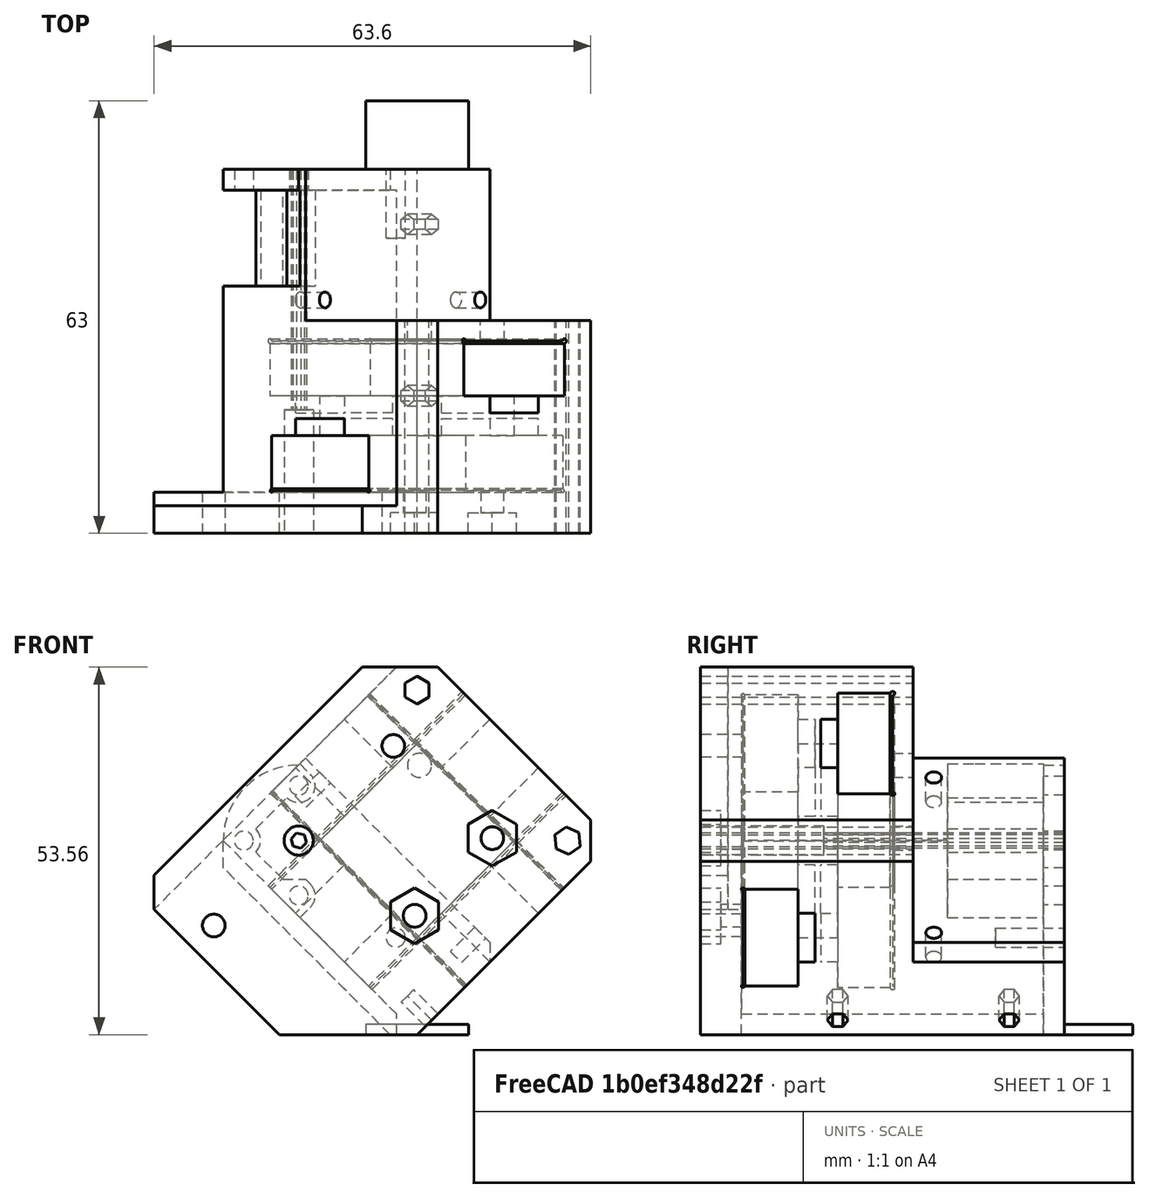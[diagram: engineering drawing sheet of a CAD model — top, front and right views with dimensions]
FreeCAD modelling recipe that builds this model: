
FCSTD DOCUMENT  (FreeCAD 0.19R)
Label: middle
License: All rights reserved
LicenseURL: http://en.wikipedia.org/wiki/All_rights_reserved
objects: Sketcher::SketchObject×25, PartDesign::Pocket×18, PartDesign::Pad×5, PartDesign::Body×1, Mesh::Feature×1
note: 72 computed .brp shape members not serialized (recipe doc carries the construction recipe); baked Part::Feature solids carry a one-line shape summary decoded from their .brp

FEATURE [Sketcher::SketchObject] Sketch  label="Body001"
  FullyConstrained = true
  MapMode = 5
  Support = -> [XY_Plane]
  sketch-geometry (11):
    g0: LineSegment StartX=20 StartY=15.7574 StartZ=0 EndX=20 EndY=-15.7574 EndZ=0
    g1: LineSegment StartX=15.7574 StartY=-20 StartZ=0 EndX=-20 EndY=-20 EndZ=0
    g2: LineSegment StartX=-20 StartY=-15.7574 StartZ=0 EndX=-20 EndY=19.9515 EndZ=0
    g3: Circle CenterX=-12.1976 CenterY=12.1976 CenterZ=0 NormalX=0 NormalY=0 NormalZ=1 AngleXU=0 Radius=2.1
    g4: LineSegment StartX=-12.1976 StartY=12.1976 StartZ=0 EndX=0 EndY=0 EndZ=0
    g5: ArcOfCircle CenterX=-12.1976 CenterY=12.1976 CenterZ=0 NormalX=0 NormalY=0 NormalZ=1 AngleXU=0 Radius=11 StartAngle=0.788519 EndAngle=2.35931
    g6: LineSegment StartX=-4.44373 StartY=20 StartZ=0 EndX=15.7574 EndY=20 EndZ=0
    g7: LineSegment StartX=15.7574 StartY=-20 StartZ=0 EndX=20 EndY=-15.7574 EndZ=0
    g8: LineSegment StartX=-20 StartY=-15.7574 StartZ=0 EndX=-22.1213 EndY=-17.8787 EndZ=0
    g9: LineSegment StartX=-22.1213 StartY=-17.8787 StartZ=0 EndX=-20 EndY=-20 EndZ=0
    g10: LineSegment StartX=15.7574 StartY=20 StartZ=0 EndX=20 EndY=15.7574 EndZ=0
  constraints (32):
    c: Horizontal(g1)
    c: Vertical(g0)
    c: Vertical(g2)
    c: Distance(g-1,g3) = 17.25
    c: Coincident(g4,g3)
    c: Coincident(g4,g-1)
    c: Angle(g4) = -0.785398
    c: Diameter(g3) = 4.2
    c: Coincident(g5,g3)
    c: Diameter(g5) = 22
    c: DistanceX(g1) = -20
    c: Coincident(g6,g5)
    c: Horizontal(g6)
    c: Coincident(g5,g2)
    c: Coincident(g7,g1)
    c: Coincident(g7,g0)
    c: Angle(g7) = 0.785398
    c: Distance(g7) = 6
    c: DistanceY(g1) = -20
    c: Coincident(g2,g8)
    c: Coincident(g8,g9)
    c: Coincident(g9,g1)
    c: Angle(g9) = -0.785398
    c: Angle(g8) = -2.35619
    c: Distance(g9) = 3
    c: DistanceX(g2) = -20
    c: Coincident(g10,g6)
    c: Coincident(g10,g0)
    c: Distance(g10) = 6
    c: Angle(g10) = -0.785398
    c: DistanceX(g0) = 20
    c: DistanceY(g6) = 20
FEATURE [PartDesign::Pad] Pad
  Direction = (1,1,1)
  Length = 53
  Length2 = 10
  Profile = -> Sketch
  Reversed = true
  Type = 0
FEATURE [Sketcher::SketchObject] Sketch001  label="RailHole"
  FullyConstrained = true
  MapMode = 5
  Placement = pos=(20,0,0) rot=(0.57735,0.57735,0.57735;2.0944rad)
  Support = -> [Pad]
  sketch-geometry (10):
    g0: LineSegment StartX=-10.35 StartY=-27.65 StartZ=0 EndX=-10.35 EndY=-20 EndZ=0
    g1: LineSegment StartX=5 StartY=-17.5 StartZ=0 EndX=-5 EndY=-17.5 EndZ=0
    g2: LineSegment StartX=10 StartY=-28 StartZ=0 EndX=-10 EndY=-28 EndZ=0
    g3: LineSegment StartX=5 StartY=-17.5 StartZ=0 EndX=5 EndY=-20 EndZ=0
    g4: LineSegment StartX=-5 StartY=-20 StartZ=0 EndX=-5 EndY=-17.5 EndZ=0
    g5: LineSegment StartX=-10.35 StartY=-20 StartZ=0 EndX=-5 EndY=-20 EndZ=0
    g6: LineSegment StartX=5 StartY=-20 StartZ=0 EndX=10.3495 EndY=-20 EndZ=0
    g7: LineSegment StartX=10.3495 StartY=-27.65 StartZ=0 EndX=10.3495 EndY=-20 EndZ=0
    g8: ArcOfCircle CenterX=-10.35 CenterY=-28 CenterZ=0 NormalX=0 NormalY=0 NormalZ=1 AngleXU=0 Radius=0.35 StartAngle=1.5708 EndAngle=6.28319
    g9: ArcOfCircle CenterX=10.35 CenterY=-28 CenterZ=0 NormalX=0 NormalY=0 NormalZ=1 AngleXU=0 Radius=0.35 StartAngle=3.14159 EndAngle=7.85541
  constraints (29):
    c: Vertical(g0)
    c: Symmetric(g1,g1,g-2)
    c: Distance(g1) = 10
    c: Coincident(g1,g3)
    c: Vertical(g3)
    c: Coincident(g4,g1)
    c: Symmetric(g3,g4,g-2)
    c: Distance(g3) = 2.5
    c: Distance(g2) = 20
    c: Coincident(g5,g4)
    c: Horizontal(g5)
    c: Coincident(g3,g6)
    c: Horizontal(g6)
    c: Vertical(g7)
    c: Coincident(g0,g5)
    c: Coincident(g7,g6)
    c: Coincident(g0,g8)
    c: Coincident(g8,g2)
    c: Diameter(g8) = 0.7
    c: DistanceX(g0,g8) = 0
    c: DistanceY(g2,g8) = 0
    c: Coincident(g9,g2)
    c: Coincident(g9,g7)
    c: Diameter(g9) = 0.7
    c: DistanceY(g2,g9) = 0
    c: DistanceX(g7,g9) = 0.0005
    c: Symmetric(g9,g8,g-2)
    c: Distance(g9,g6) = 8
    c: DistanceY(g8) = -28
FEATURE [PartDesign::Pocket] Pocket
  BaseFeature = -> Pad
  Length = 5
  Length2 = 100
  Profile = -> Sketch001
  Type = 1
FEATURE [Sketcher::SketchObject] Sketch008  label="ExtruderHole"
  FullyConstrained = false
  MapMode = 5
  Placement = pos=(0,0,4) rot=(0,0,1;0rad)
  sketch-geometry (2):
    g0: LineSegment StartX=0 StartY=0 StartZ=0 EndX=-54.6242 EndY=54.6242 EndZ=0
    g1: Circle CenterX=-12.1976 CenterY=12.1976 CenterZ=0 NormalX=0 NormalY=0 NormalZ=1 AngleXU=0 Radius=0.75
  constraints (5):
    c: Coincident(g0,g-1)
    c: Angle(g0) = 2.35619
    c: PointOnObject(g1,g0)
    c: Distance(g-1,g1) = 17.25
    c: Diameter(g1) = 1.5
FEATURE [Sketcher::SketchObject] Sketch009  label="reference"
  FullyConstrained = false
  MapMode = 5
  Placement = pos=(0,0,-25) rot=(1,0,0;3.14159rad)
  sketch-geometry (2):
    g0: Circle CenterX=-12.0208 CenterY=-12.0208 CenterZ=0 NormalX=0 NormalY=0 NormalZ=1 AngleXU=0 Radius=10
    g1: LineSegment StartX=0 StartY=0 StartZ=0 EndX=-27.7674 EndY=-27.7674 EndZ=0
  constraints (5):
    c: Diameter(g0) = 20
    c: Coincident(g1,g-1)
    c: Angle(g1) = -2.35619
    c: PointOnObject(g0,g1)
    c: Distance(g0,g1) = 17
FEATURE [Sketcher::SketchObject] Sketch010  label="reference2"
  FullyConstrained = false
  MapMode = 5
  Placement = pos=(0,0,-37) rot=(1,0,0;3.14159rad)
  sketch-geometry (2):
    g0: Circle CenterX=-12.1976 CenterY=-12.1976 CenterZ=0 NormalX=0 NormalY=0 NormalZ=1 AngleXU=0 Radius=8
    g1: LineSegment StartX=0 StartY=0 StartZ=0 EndX=-38.1566 EndY=-38.1566 EndZ=0
  constraints (5):
    c: Diameter(g0) = 16
    c: Coincident(g1,g-1)
    c: Angle(g1) = -2.35619
    c: Distance(g0,g1) = 17.25
    c: PointOnObject(g0,g1)
FEATURE [Sketcher::SketchObject] Sketch021  label="InternalTri"
  FullyConstrained = true
  MapMode = 5
  Placement = pos=(0,-3e-15,-12) rot=(0,0,1;0rad)
  sketch-geometry (4):
    g0: LineSegment StartX=-10 StartY=10 StartZ=0 EndX=10 EndY=10 EndZ=0
    g1: LineSegment StartX=10 StartY=10 StartZ=0 EndX=10 EndY=-10 EndZ=0
    g2: LineSegment StartX=10 StartY=-10 StartZ=0 EndX=-10 EndY=-10 EndZ=0
    g3: LineSegment StartX=-10 StartY=-10 StartZ=0 EndX=-10 EndY=10 EndZ=0
  constraints (11):
    c: Coincident(g0,g1)
    c: Coincident(g1,g2)
    c: Coincident(g2,g3)
    c: Coincident(g3,g0)
    c: Horizontal(g0)
    c: Horizontal(g2)
    c: Vertical(g1)
    c: Vertical(g3)
    c: Symmetric(g1,g0,g-1)
    c: Equal(g1,g0)
    c: Distance(g1) = 20
FEATURE [PartDesign::Pocket] Pocket002
  BaseFeature = -> Pocket
  Length = 10
  Length2 = 2
  Profile = -> Sketch021
  Type = 4
FEATURE [Sketcher::SketchObject] Sketch019  label="RailHole2"
  FullyConstrained = true
  MapMode = 5
  Placement = pos=(0,-20,0) rot=(1,0,0;1.5708rad)
  Support = -> [Pocket002]
  sketch-geometry (10):
    g0: LineSegment StartX=-9.75 StartY=-6.2 StartZ=0 EndX=9.75 EndY=-6.2 EndZ=0
    g1: LineSegment StartX=10 StartY=-14.2 StartZ=0 EndX=5 EndY=-14.2 EndZ=0
    g2: LineSegment StartX=5 StartY=-14.2 StartZ=0 EndX=5 EndY=-16.7 EndZ=0
    g3: LineSegment StartX=5 StartY=-16.7 StartZ=0 EndX=-5 EndY=-16.7 EndZ=0
    g4: LineSegment StartX=-5 StartY=-16.7 StartZ=0 EndX=-5 EndY=-14.2 EndZ=0
    g5: LineSegment StartX=-5 StartY=-14.2 StartZ=0 EndX=-10 EndY=-14.2 EndZ=0
    g6: ArcOfCircle CenterX=10 CenterY=-6.2 CenterZ=0 NormalX=0 NormalY=0 NormalZ=1 AngleXU=0 Radius=0.25 StartAngle=4.71239 EndAngle=9.42478
    g7: ArcOfCircle CenterX=-10 CenterY=-6.2 CenterZ=0 NormalX=0 NormalY=0 NormalZ=1 AngleXU=0 Radius=0.25 StartAngle=-9e-16 EndAngle=4.71239
    g8: LineSegment StartX=-10 StartY=-14.2 StartZ=0 EndX=-10 EndY=-6.45 EndZ=0
    g9: LineSegment StartX=10 StartY=-14.2 StartZ=0 EndX=10 EndY=-6.45 EndZ=0
  constraints (29):
    c: Horizontal(g0)
    c: Horizontal(g1)
    c: Coincident(g1,g2)
    c: Vertical(g2)
    c: Coincident(g2,g3)
    c: Horizontal(g3)
    c: Coincident(g3,g4)
    c: Vertical(g4)
    c: Coincident(g4,g5)
    c: Symmetric(g1,g5,g-2)
    c: Distance(g3) = 10
    c: Symmetric(g4,g1,g-2)
    c: DistanceY(g0) = -6.2
    c: Distance(g2) = 2.5
    c: Coincident(g6,g0)
    c: Coincident(g7,g0)
    c: Distance(g7,g6) = 20
    c: DistanceY(g1,g6) = 8
    c: Coincident(g8,g5)
    c: Vertical(g8)
    c: Coincident(g9,g1)
    c: Coincident(g9,g6)
    c: Vertical(g9)
    c: Coincident(g7,g8)
    c: Symmetric(g6,g7,g-2)
    c: Diameter(g6) = 0.5
    c: Equal(g6,g7)
    c: DistanceX(g7,g7) = 0
    c: DistanceY(g7,g0) = 0
FEATURE [Sketcher::SketchObject] Sketch024  label="hgxLITEholes"
  FullyConstrained = false
  MapMode = 5
  Placement = pos=(0,0,4) rot=(0,0,1;0rad)
  sketch-geometry (5):
    g0: Circle CenterX=7.30241 CenterY=12.1976 CenterZ=0 NormalX=0 NormalY=0 NormalZ=1 AngleXU=0 Radius=1.65
    g1: Circle CenterX=-29.6976 CenterY=12.1976 CenterZ=0 NormalX=0 NormalY=0 NormalZ=1 AngleXU=0 Radius=1.65
    g2: LineSegment StartX=-29.6976 StartY=12.1976 StartZ=0 EndX=7.30241 EndY=12.1976 EndZ=0
    g3: LineSegment StartX=0 StartY=0 StartZ=0 EndX=-27.1729 EndY=27.1729 EndZ=0
    g4: Circle CenterX=-12.1976 CenterY=12.1976 CenterZ=0 NormalX=0 NormalY=0 NormalZ=1 AngleXU=0 Radius=1.0154
  constraints (12):
    c: Diameter(g0) = 3.3
    c: Equal(g0,g1)
    c: Coincident(g2,g1)
    c: Coincident(g2,g0)
    c: Distance(g2) = 37
    c: Coincident(g3,g-1)
    c: Angle(g3) = 2.35619
    c: PointOnObject(g4,g3)
    c: Distance(g-1,g4) = 17.25
    c: Distance(g4,g0) = 19.5
    c: Horizontal(g2)
    c: PointOnObject(g4,g2)
FEATURE [PartDesign::Pocket] Pocket003
  BaseFeature = -> Pocket002
  Length = 5
  Length2 = 100
  Profile = -> Sketch019
  Type = 1
FEATURE [Sketcher::SketchObject] Sketch026  label="BottomSculp"
  FullyConstrained = false
  MapMode = 5
  Placement = pos=(0,0,-53) rot=(1,0,0;3.14159rad)
  Support = -> [Pocket003]
  sketch-geometry (5):
    g0: LineSegment StartX=29.4648 StartY=27.8981 StartZ=0 EndX=28.2209 EndY=-23.4245 EndZ=0
    g1: LineSegment StartX=28.2209 StartY=-23.4245 StartZ=0 EndX=-3.00001 EndY=-23.4245 EndZ=0
    g2: LineSegment StartX=-3.00001 StartY=-23.4245 StartZ=0 EndX=-3 EndY=18 EndZ=0
    g3: LineSegment StartX=-3 StartY=18 StartZ=0 EndX=-14.2101 EndY=29.2101 EndZ=0
    g4: LineSegment StartX=-14.2101 StartY=29.2101 StartZ=0 EndX=29.4648 EndY=27.8981 EndZ=0
  constraints (11):
    c: Coincident(g0,g1)
    c: Horizontal(g1)
    c: Coincident(g1,g2)
    c: Angle(g2) = 1.5708
    c: Coincident(g2,g3)
    c: Angle(g3) = 2.35619
    c: Coincident(g4,g3)
    c: Coincident(g4,g0)
    c: DistanceY(g2) = 18
    c: DistanceX(g2) = -3
    c: Angle(g3) = 2.35619
FEATURE [PartDesign::Pocket] Pocket004
  BaseFeature = -> Pocket003
  Length = 22
  Length2 = 100
  Profile = -> Sketch026
  Type = 0
FEATURE [Sketcher::SketchObject] Sketch004  label="Yboltpattern"
  FullyConstrained = true
  MapMode = 5
  Placement = pos=(0,0,-31) rot=(1,0,0;3.14159rad)
  Support = -> [Pocket004]
  sketch-geometry (8):
    g0: Circle CenterX=-8 CenterY=7.5 CenterZ=0 NormalX=0 NormalY=0 NormalZ=1 AngleXU=0 Radius=1.75
    g1: Circle CenterX=8 CenterY=7.5 CenterZ=0 NormalX=0 NormalY=0 NormalZ=1 AngleXU=0 Radius=1.75
    g2: Circle CenterX=-8 CenterY=-7.5 CenterZ=0 NormalX=0 NormalY=0 NormalZ=1 AngleXU=0 Radius=1.75
    g3: Circle CenterX=8 CenterY=-7.5 CenterZ=0 NormalX=0 NormalY=0 NormalZ=1 AngleXU=0 Radius=1.75
    g4: LineSegment StartX=-8 StartY=7.5 StartZ=0 EndX=8 EndY=7.5 EndZ=0
    g5: LineSegment StartX=8 StartY=7.5 StartZ=0 EndX=8 EndY=-7.5 EndZ=0
    g6: LineSegment StartX=8 StartY=-7.5 StartZ=0 EndX=-8 EndY=-7.5 EndZ=0
    g7: LineSegment StartX=-8 StartY=-7.5 StartZ=0 EndX=-8 EndY=7.5 EndZ=0
  constraints (18):
    c: Diameter(g0) = 3.5
    c: Equal(g0,g1)
    c: Equal(g0,g2)
    c: Equal(g0,g3)
    c: Distance(g2,g0) = 15
    c: Distance(g3,g2) = 16
    c: Coincident(g4,g0)
    c: Coincident(g4,g1)
    c: Coincident(g4,g5)
    c: Coincident(g5,g3)
    c: Coincident(g5,g6)
    c: Coincident(g6,g2)
    c: Coincident(g6,g7)
    c: Coincident(g7,g4)
    c: Equal(g5,g7)
    c: Equal(g4,g6)
    c: Symmetric(g1,g2,g-1)
    c: Symmetric(g0,g1,g-2)
FEATURE [Sketcher::SketchObject] Sketch022  label="VoronHoleRelif"
  FullyConstrained = true
  MapMode = 5
  Placement = pos=(0,0,-28) rot=(0,0,1;0rad)
  Support = -> [Pocket004]
  sketch-geometry (11):
    g0: ArcOfCircle CenterX=-17.8884 CenterY=6.52425 CenterZ=0 NormalX=0 NormalY=0 NormalZ=1 AngleXU=0 Radius=2.4 StartAngle=4.71239 EndAngle=6.28319
    g1: ArcOfCircle CenterX=-6.58192 CenterY=17.8307 CenterZ=0 NormalX=0 NormalY=0 NormalZ=1 AngleXU=0 Radius=2.4 StartAngle=3.14159 EndAngle=6.28319
    g2: LineSegment StartX=-22.2684 StartY=4.12425 StartZ=0 EndX=-17.8884 EndY=4.12425 EndZ=0
    g3: LineSegment StartX=-22.2684 StartY=23.8307 StartZ=0 EndX=-4.18192 EndY=23.8307 EndZ=0
    g4: LineSegment StartX=-4.18192 StartY=23.8307 StartZ=0 EndX=-4.18192 EndY=17.8307 EndZ=0
    g5: LineSegment StartX=-22.2684 StartY=4.12425 StartZ=0 EndX=-22.2684 EndY=23.8307 EndZ=0
    g6: ArcOfCircle CenterX=-17.8172 CenterY=17.8307 CenterZ=0 NormalX=0 NormalY=0 NormalZ=1 AngleXU=0 Radius=2.4 StartAngle=4.71239 EndAngle=6.28319
    g7: LineSegment StartX=-15.4172 StartY=17.8307 StartZ=0 EndX=-8.98192 EndY=17.8307 EndZ=0
    g8: LineSegment StartX=-17.8172 StartY=9.85307 StartZ=0 EndX=-15.4884 EndY=7.52425 EndZ=0
    g9: LineSegment StartX=-15.4884 StartY=6.52425 StartZ=0 EndX=-15.4884 EndY=7.52425 EndZ=0
    g10: LineSegment StartX=-17.8172 StartY=9.85307 StartZ=0 EndX=-17.8172 EndY=15.4307 EndZ=0
  constraints (33):
    c: Horizontal(g2)
    c: Coincident(g3,g4)
    c: Tangent(g4,g1) = 1.5708
    c: Tangent(g2,g0) = -1.5708
    c: Diameter(g0) = 4.8
    c: Equal(g0,g1)
    c: Vertical(g4)
    c: Horizontal(g3)
    c: Coincident(g5,g2)
    c: Coincident(g5,g3)
    c: Vertical(g5)
    c: Distance(g2) = 4.38
    c: Distance(g4) = 6
    c: DistanceX(g1) = -6.58192
    c: DistanceY(g1) = 17.8307
    c: DistanceX(g0) = -17.8884
    c: DistanceY(g0) = 6.52425
    c: Coincident(g7,g6)
    c: Coincident(g7,g1)
    c: Horizontal(g7)
    c: Perpendicular(g1,g7)
    c: Diameter(g6) = 4.8
    c: Perpendicular(g6,g7)
    c: Angle(g8) = -0.785398
    c: Vertical(g9)
    c: Tangent(g9,g0) = -1.5708
    c: Distance(g9) = 1
    c: Coincident(g8,g9)
    c: Coincident(g10,g8)
    c: Coincident(g10,g6)
    c: Vertical(g10)
    c: Perpendicular(g6,g10)
    c: DistanceX(g6) = -17.8172
FEATURE [PartDesign::Pocket] Pocket005
  BaseFeature = -> Pocket004
  Length = 22
  Length2 = -8
  Profile = -> Sketch022
  Type = 4
FEATURE [Sketcher::SketchObject] Sketch017  label="VoronHoles3"
  FullyConstrained = true
  MapMode = 5
  Placement = pos=(0,0,-50) rot=(0,0,1;0rad)
  Support = -> [Pocket005]
  sketch-geometry (10):
    g0: Circle CenterX=-6.54074 CenterY=17.8544 CenterZ=0 NormalX=0 NormalY=0 NormalZ=1 AngleXU=0 Radius=1.375
    g1: Circle CenterX=-17.8544 CenterY=6.54074 CenterZ=0 NormalX=0 NormalY=0 NormalZ=1 AngleXU=0 Radius=1.375
    g2: Circle CenterX=-6.54074 CenterY=6.54074 CenterZ=0 NormalX=0 NormalY=0 NormalZ=1 AngleXU=0 Radius=1.375
    g3: Circle CenterX=-17.8544 CenterY=17.8544 CenterZ=0 NormalX=0 NormalY=0 NormalZ=1 AngleXU=0 Radius=1.375
    g4: LineSegment StartX=-6.54074 StartY=17.8544 StartZ=0 EndX=-6.54074 EndY=6.54074 EndZ=0
    g5: LineSegment StartX=-6.54074 StartY=6.54074 StartZ=0 EndX=-17.8544 EndY=6.54074 EndZ=0
    g6: LineSegment StartX=-17.8544 StartY=6.54074 StartZ=0 EndX=-17.8544 EndY=17.8544 EndZ=0
    g7: LineSegment StartX=-17.8544 StartY=17.8544 StartZ=0 EndX=-6.54074 EndY=17.8544 EndZ=0
    g8: LineSegment StartX=0 StartY=0 StartZ=0 EndX=-37.1726 EndY=37.1726 EndZ=0
    g9: Circle CenterX=-12.1976 CenterY=12.1976 CenterZ=0 NormalX=0 NormalY=0 NormalZ=1 AngleXU=0 Radius=0.77
  constraints (25):
    c: Coincident(g4,g0)
    c: Coincident(g4,g2)
    c: Coincident(g4,g5)
    c: Coincident(g5,g1)
    c: Coincident(g5,g6)
    c: Coincident(g6,g3)
    c: Coincident(g6,g7)
    c: Coincident(g7,g4)
    c: Equal(g4,g7)
    c: Equal(g7,g6)
    c: Equal(g6,g5)
    c: Coincident(g8,g-1)
    c: PointOnObject(g9,g8)
    c: Distance(g-1,g9) = 17.25
    c: Diameter(g1) = 2.75
    c: Equal(g1,g3)
    c: Equal(g1,g0)
    c: Equal(g1,g2)
    c: Symmetric(g0,g1,g9)
    c: Distance(g2,g3) = 16
    c: Angle(g8) = 2.35619
    c: PointOnObject(g2,g8)
    c: Perpendicular(g7,g4)
    c: Distance(g8) = 52.57
    c: Diameter(g9) = 1.54
FEATURE [PartDesign::Pocket] Pocket006
  BaseFeature = -> Pocket005
  Length = 5
  Length2 = 100
  Profile = -> Sketch017
  Type = 1
FEATURE [Sketcher::SketchObject] Sketch025  label="FanDuctMountHole"
  FullyConstrained = true
  MapMode = 5
  Placement = pos=(0,0,-53) rot=(1,0,0;3.14159rad)
  Support = -> [Pocket006]
  sketch-geometry (1):
    g0: Circle CenterX=-12.2 CenterY=7.8 CenterZ=0 NormalX=0 NormalY=0 NormalZ=1 AngleXU=0 Radius=1.4
  constraints (3):
    c: Diameter(g0) = 2.8
    c: DistanceX(g0) = -12.2
    c: DistanceY(g0) = 7.8
FEATURE [PartDesign::Pocket] Pocket007
  BaseFeature = -> Pocket006
  Length = 10
  Length2 = 100
  Profile = -> Sketch025
  Type = 0
FEATURE [PartDesign::Pocket] Pocket008
  BaseFeature = -> Pocket007
  Length = 9
  Length2 = 100
  Profile = -> Sketch004
  Type = 0
FEATURE [Sketcher::SketchObject] Sketch007  label="ExtruderPlatform"
  ExternalGeometry = -> [Pad]
  FullyConstrained = false
  MapMode = 5
  Support = -> [Pocket008]
  sketch-geometry (12):
    g0: LineSegment StartX=-20 StartY=-20 StartZ=0 EndX=15.7574 EndY=-20 EndZ=0
    g1: LineSegment StartX=0 StartY=0 StartZ=0 EndX=-70.7107 EndY=70.7107 EndZ=0
    g2: Circle CenterX=-12.1976 CenterY=12.1976 CenterZ=0 NormalX=0 NormalY=0 NormalZ=1 AngleXU=0 Radius=2.125
    g3: LineSegment StartX=15.7574 StartY=-20 StartZ=0 EndX=20 EndY=-15.7574 EndZ=0
    g4: LineSegment StartX=20 StartY=-15.7574 StartZ=0 EndX=20 EndY=15.7574 EndZ=0
    g5: LineSegment StartX=20 StartY=15.7574 StartZ=0 EndX=15.7574 EndY=20 EndZ=0
    g6: LineSegment StartX=-20 StartY=-20 StartZ=0 EndX=-34.1976 EndY=-5.80241 EndZ=0
    g7: LineSegment StartX=-12.1976 StartY=-100 StartZ=0 EndX=-12.1976 EndY=100 EndZ=0
    g8: LineSegment StartX=-34.1976 StartY=-5.80241 StartZ=0 EndX=-34.1976 EndY=20 EndZ=0
    g9: LineSegment StartX=-34.1976 StartY=20 StartZ=0 EndX=15.7574 EndY=20 EndZ=0
    g10: Circle CenterX=-29.6976 CenterY=12.1976 CenterZ=0 NormalX=0 NormalY=0 NormalZ=1 AngleXU=0 Radius=1.4
    g11: Circle CenterX=7.30241 CenterY=11.9057 CenterZ=0 NormalX=0 NormalY=0 NormalZ=1 AngleXU=0 Radius=1.4
  constraints (35):
    c: Coincident(g1,g-1)
    c: Angle(g1) = 2.35619
    c: Diameter(g2) = 4.25
    c: PointOnObject(g2,g1)
    c: Distance(g-1,g2) = 17.25
    c: Coincident(g0,g3)
    c: Coincident(g3,g4)
    c: Coincident(g6,g0)
    c: Angle(g6) = 2.35619
    c: Coincident(g5,g4)
    c: Distance(g1) = 100
    c: PointOnObject(g2,g7)
    c: DistanceX(g0,g0) = -35.7574
    c: DistanceY(g0,g0) = 0
    c: DistanceX(g3,g0) = -40
    c: DistanceY(g3,g0) = -4.24264
    c: DistanceX(g4) = 20
    c: DistanceY(g4) = 15.7574
    c: DistanceX(g3) = 20
    c: DistanceY(g3) = -15.7574
    c: Coincident(g8,g6)
    c: Vertical(g8)
    c: Horizontal(g9)
    c: Coincident(g5,g9)
    c: Distance(g8,g7) = 22
    c: DistanceX(g5) = 15.7574
    c: DistanceY(g5) = 20
    c: Symmetric(g7,g7,g-1)
    c: Distance(g7) = 200
    c: DistanceX(g10,g2) = 17.5
    c: DistanceX(g2,g11) = 19.5
    c: Diameter(g10) = 2.8
    c: Equal(g10,g11)
    c: DistanceY(g10,g2) = 0
    c: Coincident(g9,g8)
FEATURE [PartDesign::Pad] Pad001
  BaseFeature = -> Pocket008
  Direction = (1,1,1)
  Length = 6
  Length2 = 100
  Profile = -> Sketch007
  Reversed = true
  Type = 0
FEATURE [PartDesign::Pocket] Pocket009
  BaseFeature = -> Pad001
  Length = 11
  Length2 = 100
  Profile = -> Sketch024
  Type = 0
FEATURE [PartDesign::Pocket] Pocket010
  BaseFeature = -> Pocket009
  Length = 5
  Length2 = 100
  Profile = -> Sketch008
  Type = 1
FEATURE [Sketcher::SketchObject] Sketch003  label="Xboltpattern"
  FullyConstrained = true
  MapMode = 5
  Support = -> [Pocket010]
  sketch-geometry (8):
    g0: Circle CenterX=-8 CenterY=7.5 CenterZ=0 NormalX=0 NormalY=0 NormalZ=1 AngleXU=0 Radius=1.65
    g1: Circle CenterX=8 CenterY=7.5 CenterZ=0 NormalX=0 NormalY=0 NormalZ=1 AngleXU=0 Radius=1.65
    g2: Circle CenterX=-8 CenterY=-7.5 CenterZ=0 NormalX=0 NormalY=0 NormalZ=1 AngleXU=0 Radius=1.65
    g3: Circle CenterX=8 CenterY=-7.5 CenterZ=0 NormalX=0 NormalY=0 NormalZ=1 AngleXU=0 Radius=1.65
    g4: LineSegment StartX=-8 StartY=7.5 StartZ=0 EndX=8 EndY=7.5 EndZ=0
    g5: LineSegment StartX=8 StartY=7.5 StartZ=0 EndX=8 EndY=-7.5 EndZ=0
    g6: LineSegment StartX=8 StartY=-7.5 StartZ=0 EndX=-8 EndY=-7.5 EndZ=0
    g7: LineSegment StartX=-8 StartY=-7.5 StartZ=0 EndX=-8 EndY=7.5 EndZ=0
  constraints (19):
    c: Diameter(g0) = 3.3
    c: Equal(g0,g1)
    c: Equal(g0,g2)
    c: Equal(g0,g3)
    c: Distance(g0,g1) = 16
    c: Distance(g1,g3) = 15
    c: Coincident(g4,g0)
    c: Coincident(g4,g1)
    c: Horizontal(g4)
    c: Coincident(g4,g5)
    c: Coincident(g5,g3)
    c: Vertical(g5)
    c: Coincident(g5,g6)
    c: Coincident(g6,g2)
    c: Coincident(g6,g7)
    c: Coincident(g7,g4)
    c: Symmetric(g2,g1,g-1)
    c: Equal(g7,g5)
    c: Equal(g6,g4)
FEATURE [Sketcher::SketchObject] Sketch029  label="Adhesion"
  FullyConstrained = false
  MapMode = 5
  Placement = pos=(0,0,-53) rot=(1,0,0;3.14159rad)
  sketch-geometry (4):
    g0: LineSegment StartX=-13.636 StartY=24.2426 StartZ=0 EndX=-24.2426 EndY=13.636 EndZ=0
    g1: LineSegment StartX=-24.2426 StartY=13.636 StartZ=0 EndX=-25.3033 EndY=14.6967 EndZ=0
    g2: LineSegment StartX=-25.3033 StartY=14.6967 StartZ=0 EndX=-14.6967 EndY=25.3033 EndZ=0
    g3: LineSegment StartX=-14.6967 StartY=25.3033 StartZ=0 EndX=-13.636 EndY=24.2426 EndZ=0
  constraints (10):
    c: Coincident(g0,g1)
    c: Coincident(g1,g2)
    c: Coincident(g2,g3)
    c: Coincident(g3,g0)
    c: Angle(g2) = 0.785398
    c: Distance(g2) = 15
    c: Distance(g1) = 1.5
    c: Distance(g3) = 1.5
    c: Perpendicular(g2,g3)
    c: Perpendicular(g2,g1)
FEATURE [Sketcher::SketchObject] Sketch033  label="WireMgmnt"
  FullyConstrained = true
  MapMode = 5
  Placement = pos=(0,-20,0) rot=(1,0,0;1.5708rad)
  sketch-geometry (14):
    g0: LineSegment StartX=-15.7 StartY=-20.7506 StartZ=0 EndX=-15.7 EndY=-19.2494 EndZ=0
    g1: LineSegment StartX=-15.7 StartY=-19.2494 StartZ=0 EndX=-17 EndY=-18.4989 EndZ=0
    g2: LineSegment StartX=-17 StartY=-18.4989 StartZ=0 EndX=-18.3 EndY=-19.2494 EndZ=0
    g3: LineSegment StartX=-18.3 StartY=-19.2494 StartZ=0 EndX=-18.3 EndY=-20.7506 EndZ=0
    g4: LineSegment StartX=-18.3 StartY=-20.7506 StartZ=0 EndX=-17 EndY=-21.5011 EndZ=0
    g5: LineSegment StartX=-17 StartY=-21.5011 StartZ=0 EndX=-15.7 EndY=-20.7506 EndZ=0
    g6: Circle CenterX=-17 CenterY=-20 CenterZ=0 NormalX=0 NormalY=0 NormalZ=1 AngleXU=0 Radius=1.50111
    g7: LineSegment StartX=-15.7 StartY=-44.2494 StartZ=0 EndX=-17 EndY=-43.4989 EndZ=0
    g8: LineSegment StartX=-17 StartY=-43.4989 StartZ=0 EndX=-18.3 EndY=-44.2494 EndZ=0
    g9: LineSegment StartX=-18.3 StartY=-44.2494 StartZ=0 EndX=-18.3 EndY=-45.7506 EndZ=0
    g10: LineSegment StartX=-18.3 StartY=-45.7506 StartZ=0 EndX=-17 EndY=-46.5011 EndZ=0
    g11: LineSegment StartX=-17 StartY=-46.5011 StartZ=0 EndX=-15.7 EndY=-45.7506 EndZ=0
    g12: LineSegment StartX=-15.7 StartY=-45.7506 StartZ=0 EndX=-15.7 EndY=-44.2494 EndZ=0
    g13: Circle CenterX=-17 CenterY=-45 CenterZ=0 NormalX=0 NormalY=0 NormalZ=1 AngleXU=0 Radius=1.50111
  constraints (34):
    c: Coincident(g0,g1)
    c: Coincident(g1,g2)
    c: Coincident(g2,g3)
    c: Coincident(g3,g4)
    c: Coincident(g4,g5)
    c: Coincident(g5,g0)
    c: Equal(g0, g1-g5) x5
    c: PointOnObject(g0,g6)
    c: PointOnObject(g1,g6)
    c: PointOnObject(g2,g6)
    c: PointOnObject(g3,g6)
    c: PointOnObject(g4,g6)
    c: PointOnObject(g5,g6)
    c: Coincident(g7,g8)
    c: Coincident(g8,g9)
    c: Coincident(g9,g10)
    c: Coincident(g10,g11)
    c: Coincident(g11,g12)
    c: Coincident(g12,g7)
    c: Equal(g7, g8-g12) x5
    c: PointOnObject(g7,g13)
    c: PointOnObject(g8,g13)
    c: PointOnObject(g9,g13)
    c: PointOnObject(g10,g13)
    c: PointOnObject(g11,g13)
    c: PointOnObject(g12,g13)
    c: DistanceX(g13) = -17
    c: Distance(g10,g7) = 2.6
    c: Vertical(g9)
    c: DistanceY(g13) = -45
    c: Distance(g3,g0) = 2.6
    c: DistanceY(g6) = -20
    c: Vertical(g3)
    c: DistanceX(g6) = -17
FEATURE [Sketcher::SketchObject] Sketch035  label="Bottom Reinforce"
  FullyConstrained = false
  MapMode = 5
  Placement = pos=(0,0,-53) rot=(1,0,0;3.14159rad)
  sketch-geometry (4):
    g0: LineSegment StartX=-22.779 StartY=17.221 StartZ=0 EndX=-22.779 EndY=-17.1725 EndZ=0
    g1: LineSegment StartX=-22.779 StartY=-17.1725 StartZ=0 EndX=-20 EndY=-19.9515 EndZ=0
    g2: LineSegment StartX=-20 StartY=-19.9515 StartZ=0 EndX=-20 EndY=20 EndZ=0
    g3: LineSegment StartX=-20 StartY=20 StartZ=0 EndX=-22.779 EndY=17.221 EndZ=0
  constraints (9):
    c: Vertical(g0)
    c: Coincident(g0,g1)
    c: Coincident(g1,g2)
    c: Vertical(g2)
    c: Coincident(g2,g3)
    c: Coincident(g3,g0)
    c: Angle(g1) = -0.785398
    c: DistanceY(g2) = 20
    c: Angle(g3) = -2.35619
FEATURE [Sketcher::SketchObject] Sketch037  label="BumpTrim"
  FullyConstrained = false
  MapMode = 5
  sketch-geometry (4):
    g0: LineSegment StartX=-26.2848 StartY=31.2083 StartZ=0 EndX=-1.26106 EndY=31.2083 EndZ=0
    g1: LineSegment StartX=-1.26106 StartY=31.2083 StartZ=0 EndX=-1.26106 EndY=20 EndZ=0
    g2: LineSegment StartX=-1.26106 StartY=20 StartZ=0 EndX=-26.2848 EndY=20 EndZ=0
    g3: LineSegment StartX=-26.2848 StartY=20 StartZ=0 EndX=-26.2848 EndY=31.2083 EndZ=0
  constraints (9):
    c: Coincident(g0,g1)
    c: Coincident(g1,g2)
    c: Coincident(g2,g3)
    c: Coincident(g3,g0)
    c: Horizontal(g0)
    c: Horizontal(g2)
    c: Vertical(g1)
    c: Vertical(g3)
    c: DistanceY(g1) = 20
FEATURE [PartDesign::Pocket] Pocket011
  BaseFeature = -> Pocket010
  Length = 10
  Length2 = 100
  Profile = -> Sketch003
  Type = 0
FEATURE [Sketcher::SketchObject] Sketch036  label="countersink"
  FullyConstrained = true
  MapMode = 5
  Support = -> [Pocket011]
  sketch-geometry (14):
    g0: LineSegment StartX=11.9037 StartY=-8.546 StartZ=0 EndX=10.8577 EndY=-4.64226 EndZ=0
    g1: LineSegment StartX=10.8577 StartY=-4.64226 StartZ=0 EndX=6.954 EndY=-3.59626 EndZ=0
    g2: LineSegment StartX=6.954 StartY=-3.59626 StartZ=0 EndX=4.09626 EndY=-6.454 EndZ=0
    g3: LineSegment StartX=4.09626 StartY=-6.454 StartZ=0 EndX=5.14226 EndY=-10.3577 EndZ=0
    g4: LineSegment StartX=5.14226 StartY=-10.3577 StartZ=0 EndX=9.046 EndY=-11.4037 EndZ=0
    g5: LineSegment StartX=9.046 StartY=-11.4037 StartZ=0 EndX=11.9037 EndY=-8.546 EndZ=0
    g6: Circle CenterX=8 CenterY=-7.5 CenterZ=0 NormalX=0 NormalY=0 NormalZ=1 AngleXU=0 Radius=4.04145
    g7: LineSegment StartX=-5.14226 StartY=-4.64226 StartZ=0 EndX=-9.046 EndY=-3.59626 EndZ=0
    g8: LineSegment StartX=-9.046 StartY=-3.59626 StartZ=0 EndX=-11.9037 EndY=-6.454 EndZ=0
    g9: LineSegment StartX=-11.9037 StartY=-6.454 StartZ=0 EndX=-10.8577 EndY=-10.3577 EndZ=0
    g10: LineSegment StartX=-10.8577 StartY=-10.3577 StartZ=0 EndX=-6.954 EndY=-11.4037 EndZ=0
    g11: LineSegment StartX=-6.954 StartY=-11.4037 StartZ=0 EndX=-4.09626 EndY=-8.546 EndZ=0
    g12: LineSegment StartX=-4.09626 StartY=-8.546 StartZ=0 EndX=-5.14226 EndY=-4.64226 EndZ=0
    g13: Circle CenterX=-8 CenterY=-7.5 CenterZ=0 NormalX=0 NormalY=0 NormalZ=1 AngleXU=0 Radius=4.04145
  constraints (34):
    c: Coincident(g0,g1)
    c: Coincident(g1,g2)
    c: Coincident(g2,g3)
    c: Coincident(g3,g4)
    c: Coincident(g4,g5)
    c: Coincident(g5,g0)
    c: Equal(g0, g1-g5) x5
    c: PointOnObject(g0,g6)
    c: PointOnObject(g1,g6)
    c: PointOnObject(g2,g6)
    c: PointOnObject(g3,g6)
    c: PointOnObject(g4,g6)
    c: PointOnObject(g5,g6)
    c: Coincident(g7,g8)
    c: Coincident(g8,g9)
    c: Coincident(g9,g10)
    c: Coincident(g10,g11)
    c: Coincident(g11,g12)
    c: Coincident(g12,g7)
    c: Equal(g7, g8-g12) x5
    c: PointOnObject(g7,g13)
    c: PointOnObject(g8,g13)
    c: PointOnObject(g9,g13)
    c: PointOnObject(g10,g13)
    c: PointOnObject(g11,g13)
    c: PointOnObject(g12,g13)
    c: Angle(g11) = 0.785398
    c: Angle(g5) = 0.785398
    c: Distance(g0,g2) = 7
    c: Distance(g7,g8) = 7
    c: DistanceX(g6) = 8
    c: DistanceY(g6) = -7.5
    c: DistanceY(g13) = -7.5
    c: DistanceX(g13) = -8
FEATURE [PartDesign::Pocket] Pocket012
  BaseFeature = -> Pocket011
  Length = 3
  Length2 = 100
  Profile = -> Sketch036
  Type = 0
FEATURE [PartDesign::Pocket] Pocket013
  BaseFeature = -> Pocket012
  Length = 5
  Length2 = 100
  Profile = -> Sketch033
  Type = 0
FEATURE [PartDesign::Pad] Pad002
  BaseFeature = -> Pocket013
  Direction = (1,1,1)
  Length = 3
  Length2 = 100
  Profile = -> Sketch035
  Reversed = true
  Type = 0
FEATURE [PartDesign::Pocket] Pocket014
  BaseFeature = -> Pad002
  Length = 40
  Length2 = 100
  Profile = -> Sketch037
  Type = 0
FEATURE [PartDesign::Pad] Pad003
  BaseFeature = -> Pocket014
  Direction = (1,1,1)
  Length = 10
  Length2 = 100
  Profile = -> Sketch029
  Type = 0
FEATURE [Sketcher::SketchObject] Sketch039  label="platformBump"
  ExternalGeometry = -> [Pad003]
  FullyConstrained = true
  MapMode = 5
  Support = -> [Pad003]
  sketch-geometry (4):
    g0: LineSegment StartX=-30.6621 StartY=23.5355 StartZ=0 EndX=12.2218 EndY=23.5355 EndZ=0
    g1: LineSegment StartX=12.2218 StartY=23.5355 StartZ=0 EndX=15.7574 EndY=20 EndZ=0
    g2: LineSegment StartX=15.7574 StartY=20 StartZ=0 EndX=-34.1976 EndY=20 EndZ=0
    g3: LineSegment StartX=-34.1976 StartY=20 StartZ=0 EndX=-30.6621 EndY=23.5355 EndZ=0
  constraints (10):
    c: Coincident(g0,g1)
    c: Coincident(g1,g2)
    c: Coincident(g2,g3)
    c: Coincident(g3,g0)
    c: Horizontal(g0)
    c: Distance(g1) = 5
    c: Coincident(g2,g-3)
    c: Coincident(g1,g-4)
    c: Angle(g1) = -0.785398
    c: Angle(g3) = 0.785398
FEATURE [PartDesign::Pad] Pad004
  BaseFeature = -> Pad003
  Direction = (1,1,1)
  Length = 4
  Length2 = 100
  Profile = -> Sketch039
  Reversed = true
  Type = 0
FEATURE [Sketcher::SketchObject] Sketch040  label="WireHoles"
  FullyConstrained = true
  MapMode = 5
  Support = -> [Pad004]
  sketch-geometry (21):
    g0: LineSegment StartX=16.1911 StartY=-17.3989 StartZ=0 EndX=17.49 EndY=-15.8509 EndZ=0
    g1: LineSegment StartX=17.49 StartY=-15.8509 StartZ=0 EndX=16.7989 EndY=-13.952 EndZ=0
    g2: LineSegment StartX=16.7989 StartY=-13.952 StartZ=0 EndX=14.8089 EndY=-13.6011 EndZ=0
    g3: LineSegment StartX=14.8089 StartY=-13.6011 StartZ=0 EndX=13.51 EndY=-15.1491 EndZ=0
    g4: LineSegment StartX=13.51 StartY=-15.1491 StartZ=0 EndX=14.2011 EndY=-17.048 EndZ=0
    g5: LineSegment StartX=14.2011 StartY=-17.048 StartZ=0 EndX=16.1911 EndY=-17.3989 EndZ=0
    g6: Circle CenterX=15.5 CenterY=-15.5 CenterZ=0 NormalX=0 NormalY=0 NormalZ=1 AngleXU=0 Radius=2.02073
    g7: LineSegment StartX=14.977 StartY=17.4519 StartZ=0 EndX=13.5481 EndY=16.023 EndZ=0
    g8: LineSegment StartX=13.5481 StartY=16.023 StartZ=0 EndX=14.0711 EndY=14.0711 EndZ=0
    g9: LineSegment StartX=14.0711 StartY=14.0711 StartZ=0 EndX=16.023 EndY=13.5481 EndZ=0
    g10: LineSegment StartX=16.023 StartY=13.5481 StartZ=0 EndX=17.4519 EndY=14.977 EndZ=0
    g11: LineSegment StartX=17.4519 StartY=14.977 StartZ=0 EndX=16.9289 EndY=16.9289 EndZ=0
    g12: LineSegment StartX=16.9289 StartY=16.9289 StartZ=0 EndX=14.977 EndY=17.4519 EndZ=0
    g13: Circle CenterX=15.5 CenterY=15.5 CenterZ=0 NormalX=0 NormalY=0 NormalZ=1 AngleXU=0 Radius=2.02073
    g14: LineSegment StartX=-14.7753 StartY=-17.2247 StartZ=0 EndX=-14.327 EndY=-15.5517 EndZ=0
    g15: LineSegment StartX=-14.327 StartY=-15.5517 StartZ=0 EndX=-15.5517 EndY=-14.327 EndZ=0
    g16: LineSegment StartX=-15.5517 StartY=-14.327 StartZ=0 EndX=-17.2247 EndY=-14.7753 EndZ=0
    g17: LineSegment StartX=-17.2247 StartY=-14.7753 StartZ=0 EndX=-17.673 EndY=-16.4483 EndZ=0
    g18: LineSegment StartX=-17.673 StartY=-16.4483 StartZ=0 EndX=-16.4483 EndY=-17.673 EndZ=0
    g19: LineSegment StartX=-16.4483 StartY=-17.673 StartZ=0 EndX=-14.7753 EndY=-17.2247 EndZ=0
    g20: Circle CenterX=-16 CenterY=-16 CenterZ=0 NormalX=0 NormalY=0 NormalZ=1 AngleXU=0 Radius=1.73205
  constraints (51):
    c: Coincident(g0,g1)
    c: Coincident(g1,g2)
    c: Coincident(g2,g3)
    c: Coincident(g3,g4)
    c: Coincident(g4,g5)
    c: Coincident(g5,g0)
    c: Equal(g0, g1-g5) x5
    c: PointOnObject(g0,g6)
    c: PointOnObject(g1,g6)
    c: PointOnObject(g2,g6)
    c: PointOnObject(g3,g6)
    c: PointOnObject(g4,g6)
    c: PointOnObject(g5,g6)
    c: Coincident(g7,g8)
    c: Coincident(g8,g9)
    c: Coincident(g9,g10)
    c: Coincident(g10,g11)
    c: Coincident(g11,g12)
    c: Coincident(g12,g7)
    c: Equal(g7, g8-g12) x5
    c: PointOnObject(g7,g13)
    c: PointOnObject(g8,g13)
    c: PointOnObject(g9,g13)
    c: PointOnObject(g10,g13)
    c: PointOnObject(g11,g13)
    c: PointOnObject(g12,g13)
    c: Distance(g0,g4) = 3.5
    c: Distance(g7,g11) = 3.5
    c: DistanceX(g13) = 15.5
    c: DistanceY(g13) = 15.5
    c: DistanceX(g6) = 15.5
    c: DistanceY(g6) = -15.5
    c: Coincident(g14,g15)
    c: Coincident(g15,g16)
    c: Coincident(g16,g17)
    c: Coincident(g17,g18)
    c: Coincident(g18,g19)
    c: Coincident(g19,g14)
    c: Equal(g14, g15-g19) x5
    c: PointOnObject(g14,g20)
    c: PointOnObject(g15,g20)
    c: PointOnObject(g16,g20)
    c: PointOnObject(g17,g20)
    c: PointOnObject(g18,g20)
    c: PointOnObject(g19,g20)
    c: Distance(g18,g14) = 3
    c: Angle(g15) = 2.35619
    c: DistanceX(g20) = -16
    c: DistanceY(g20) = -16
    c: Angle(g3) = -2.26893
    c: Angle(g11) = 1.8326
FEATURE [PartDesign::Pocket] Pocket015
  BaseFeature = -> Pad004
  Length = 5
  Length2 = 100
  Profile = -> Sketch040
  Type = 1
FEATURE [Sketcher::SketchObject] Sketch041  label="PCBmountholes"
  FullyConstrained = true
  MapMode = 5
  Placement = pos=(-3.00001,-9.80387e-07,0) rot=(0.57735,0.57735,0.57735;2.0944rad)
  Support = -> [Pocket015]
  sketch-geometry (2):
    g0: Circle CenterX=16 CenterY=-34 CenterZ=0 NormalX=0 NormalY=0 NormalZ=1 AngleXU=0 Radius=1.15
    g1: Circle CenterX=-16 CenterY=-34 CenterZ=0 NormalX=0 NormalY=0 NormalZ=1 AngleXU=0 Radius=1.15
  constraints (5):
    c: Distance(g0,g1) = 32
    c: Symmetric(g1,g0,g-2)
    c: Diameter(g0) = 2.3
    c: Equal(g0,g1)
    c: DistanceY(g1) = -34
FEATURE [PartDesign::Pocket] Pocket016
  BaseFeature = -> Pocket015
  Length = 5
  Length2 = 100
  Profile = -> Sketch041
  Type = 0
FEATURE [Sketcher::SketchObject] Sketch042
  FullyConstrained = true
  MapMode = 5
  Placement = pos=(0,0,-53) rot=(1,0,0;3.14159rad)
  Support = -> [Pocket014]
  sketch-geometry (7):
    g0: LineSegment StartX=-13.3547 StartY=-12.2 StartZ=0 EndX=-12.7774 EndY=-13.2 EndZ=0
    g1: LineSegment StartX=-12.7774 StartY=-13.2 StartZ=0 EndX=-11.6226 EndY=-13.2 EndZ=0
    g2: LineSegment StartX=-11.6226 StartY=-13.2 StartZ=0 EndX=-11.0453 EndY=-12.2 EndZ=0
    g3: LineSegment StartX=-11.0453 StartY=-12.2 StartZ=0 EndX=-11.6226 EndY=-11.2 EndZ=0
    g4: LineSegment StartX=-11.6226 StartY=-11.2 StartZ=0 EndX=-12.7774 EndY=-11.2 EndZ=0
    g5: LineSegment StartX=-12.7774 StartY=-11.2 StartZ=0 EndX=-13.3547 EndY=-12.2 EndZ=0
    g6: Circle CenterX=-12.2 CenterY=-12.2 CenterZ=0 NormalX=0 NormalY=0 NormalZ=1 AngleXU=0 Radius=1.1547
  constraints (17):
    c: Coincident(g0,g1)
    c: Coincident(g1,g2)
    c: Coincident(g2,g3)
    c: Coincident(g3,g4)
    c: Coincident(g4,g5)
    c: Coincident(g5,g0)
    c: Equal(g0, g1-g5) x5
    c: PointOnObject(g0,g6)
    c: PointOnObject(g1,g6)
    c: PointOnObject(g2,g6)
    c: PointOnObject(g3,g6)
    c: PointOnObject(g4,g6)
    c: PointOnObject(g5,g6)
    c: DistanceX(g6) = -12.2
    c: DistanceY(g6) = -12.2
    c: Distance(g0,g4) = 2
    c: Angle(g1) = 0
FEATURE [PartDesign::Pocket] Pocket017
  BaseFeature = -> Pocket016
  Length = 5
  Length2 = 100
  Profile = -> Sketch042
  Type = 1
FEATURE [Sketcher::SketchObject] Sketch043
  FullyConstrained = true
  MapMode = 5
  Support = -> [Pocket017]
  sketch-geometry (1):
    g0: Circle CenterX=-12.2 CenterY=12.2 CenterZ=0 NormalX=0 NormalY=0 NormalZ=1 AngleXU=0 Radius=2.125
  constraints (3):
    c: DistanceX(g0) = -12.2
    c: DistanceY(g0) = 12.2
    c: Diameter(g0) = 4.25
FEATURE [PartDesign::Pocket] Pocket018
  BaseFeature = -> Pocket017
  Length = 18
  Length2 = 100
  Profile = -> Sketch043
  Type = 0
FEATURE [PartDesign::Body] Body
  Group = -> [Sketch,Pad,Sketch001,Pocket,Sketch003,Sketch004,Sketch007,Sketch008,Sketch009,Sketch010,Sketch017,Sketch019,Sketch021,Pocket002,Sketch022,Sketch024,Sketch025,Sketch026,Pocket003,Pocket004,Pocket005,Pocket006,Pocket007,Pocket008,Pad001,Pocket009,Pocket010,Sketch029,Sketch033,Sketch035,Sketch036,Sketch037,Pocket011,Pocket012,Pocket013,Pad002,Pocket014,Pad003,Sketch039,Pad004,Sketch040,Pocket015,+6 more]
  Origin = -> Origin
  Placement = pos=(0,0,0) rot=(0.862856,-0.357407,0.357407;1.71777rad)
  Tip = -> Pocket018
FEATURE [Mesh::Feature] Mesh  label="Pocket018 (Meshed)"
